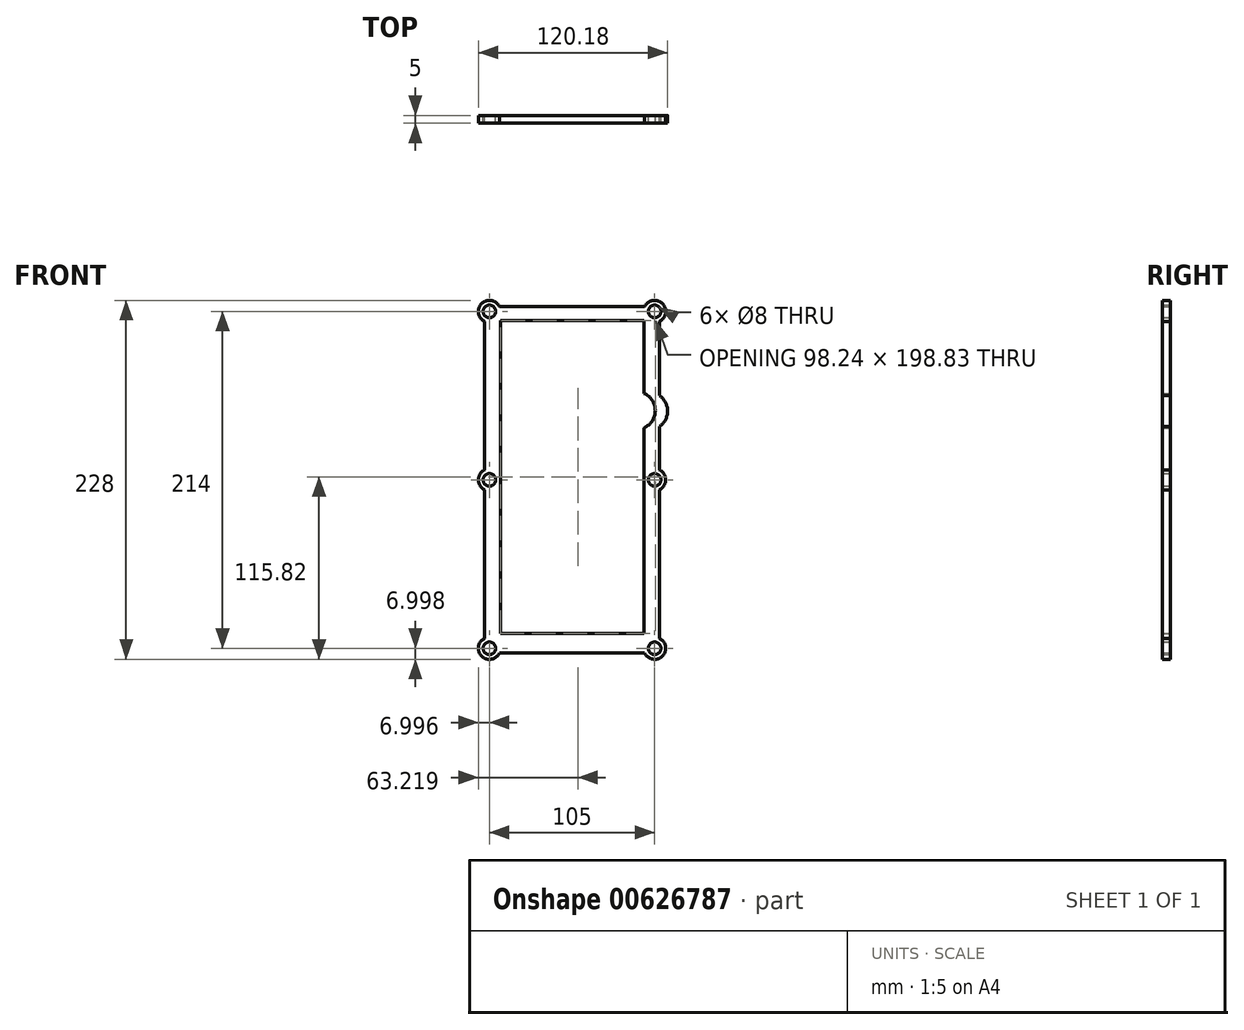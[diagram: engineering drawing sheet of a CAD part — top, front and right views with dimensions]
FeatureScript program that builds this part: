
annotation { "Feature Type Name" : "Feature", "Feature Type Description" : "" }
export const myFeature = defineFeature(function(context is Context, id is Id, definition is map)
    precondition{}
    {
        {
            var Q0;
            Q0=qCreatedBy(makeId("Front.planeOp"),FACE);
            var sketch = newSketch(context, id + "F0", { "sketchPlane" : qUnion([Q0])});
            skLineSegment(sketch, "E0.bottom", {"start": v(-54.77, 95.48) * mm, "end": v(50.23, 95.48) * mm, "construction": true});
            skLineSegment(sketch, "E0.top", {"start": v(-54.77, -118.52) * mm, "end": v(50.23, -118.52) * mm, "construction": true});
            skLineSegment(sketch, "E0.left", {"start": v(-54.77, 95.48) * mm, "end": v(-54.77, -118.52) * mm, "construction": true});
            skLineSegment(sketch, "E0.right", {"start": v(50.23, 95.48) * mm, "end": v(50.23, -118.52) * mm, "construction": true});
            skCircle(sketch, "E1", {"center": v(-54.77, 95.48) * mm, "radius": 4 * mm});
            skCircle(sketch, "E2", {"center": v(50.23, 95.48) * mm, "radius": 4 * mm});
            skCircle(sketch, "E3", {"center": v(50.23, -11.52) * mm, "radius": 4 * mm});
            skCircle(sketch, "E4", {"center": v(50.23, -118.52) * mm, "radius": 4 * mm});
            skCircle(sketch, "E5", {"center": v(-54.77, -118.52) * mm, "radius": 4 * mm});
            skCircle(sketch, "E6", {"center": v(-54.77, -11.52) * mm, "radius": 4 * mm});
            skPoint(sketch, "E7.middle", {"position": v(0, -10.99) * mm});
            skArc(sketch, "E8", {"start": v(-57.77, -112.2) * mm, "mid": v(-59.72, -123.47) * mm, "end": v(-48.45, -121.52) * mm});
            skArc(sketch, "E9", {"start": v(-48.45, 98.48) * mm, "mid": v(-59.72, 100.43) * mm, "end": v(-57.77, 89.15) * mm});
            skArc(sketch, "E10", {"start": v(53.23, 89.15) * mm, "mid": v(55.18, 100.43) * mm, "end": v(43.9, 98.48) * mm});
            skArc(sketch, "E11", {"start": v(53.23, -17.85) * mm, "mid": v(57.23, -11.52) * mm, "end": v(53.23, -5.2) * mm});
            skArc(sketch, "E12", {"start": v(-57.77, -5.2) * mm, "mid": v(-61.77, -11.52) * mm, "end": v(-57.77, -17.85) * mm});
            skArc(sketch, "E13", {"start": v(43.9, -121.52) * mm, "mid": v(55.18, -123.47) * mm, "end": v(53.23, -112.2) * mm});
            skLineSegment(sketch, "E14", {"start": v(-48.45, 98.48) * mm, "end": v(43.9, 98.48) * mm});
            skLineSegment(sketch, "E15", {"start": v(-57.77, 89.15) * mm, "end": v(-57.77, -5.2) * mm});
            skLineSegment(sketch, "E16", {"start": v(53.23, 89.15) * mm, "end": v(53.23, 42.02) * mm});
            skLineSegment(sketch, "E17", {"start": v(53.23, -17.85) * mm, "end": v(53.23, -112.2) * mm});
            skLineSegment(sketch, "E18", {"start": v(-57.77, -17.85) * mm, "end": v(-57.77, -112.2) * mm});
            skLineSegment(sketch, "E19", {"start": v(-48.45, -121.52) * mm, "end": v(43.9, -121.52) * mm});
            skLineSegment(sketch, "E20", {"start": v(30.5, 32.48) * mm, "end": v(50.23, 32.48) * mm, "construction": true});
            skArc(sketch, "E21", {"start": v(53.23, 22.3) * mm, "mid": v(58.4, 32.16) * mm, "end": v(53.23, 42.02) * mm});
            skLineSegment(sketch, "E22.trimOffspring", {"start": v(53.23, 22.3) * mm, "end": v(53.23, -5.2) * mm});
            skLineSegment(sketch, "E23.bottom", {"start": v(-47.67, 89.71) * mm, "end": v(43.57, 89.71) * mm});
            skLineSegment(sketch, "E23.top", {"start": v(-47.67, -109.11) * mm, "end": v(43.57, -109.11) * mm});
            skLineSegment(sketch, "E23.left", {"start": v(-47.67, 89.71) * mm, "end": v(-47.67, -109.11) * mm});
            skLineSegment(sketch, "E23.right", {"start": v(43.57, 89.71) * mm, "end": v(43.57, 43.39) * mm});
            skLineSegment(sketch, "E24", {"start": v(40.36, 32.48) * mm, "end": v(38.57, 32.48) * mm, "construction": true});
            skArc(sketch, "E25", {"start": v(43.57, 21.57) * mm, "mid": v(50.57, 32.48) * mm, "end": v(43.57, 43.39) * mm});
            skLineSegment(sketch, "E26.trimOffspring", {"start": v(43.57, 21.57) * mm, "end": v(43.57, -109.11) * mm});
            skSolve(sketch);
        }
        {
            var Q0;
            Q0=makeQuery(id+"F0.imprint","IMPRINT",FACE,{"disambiguationData":[TD([[makeQuery(id+"F0.imprint","IMPRINT",EDGE,{"derivedFrom":sQuery(id+"F0.wireOp",EDGE,"E1")}),-1.0]])]});
            extrude(context, id + "F1", {"entities" : qUnion([Q0]), "endBound" : BoundingType.SYMMETRIC, "depth" : 5 * mm, "offsetDistance" : 25 * mm});
        }
    });
